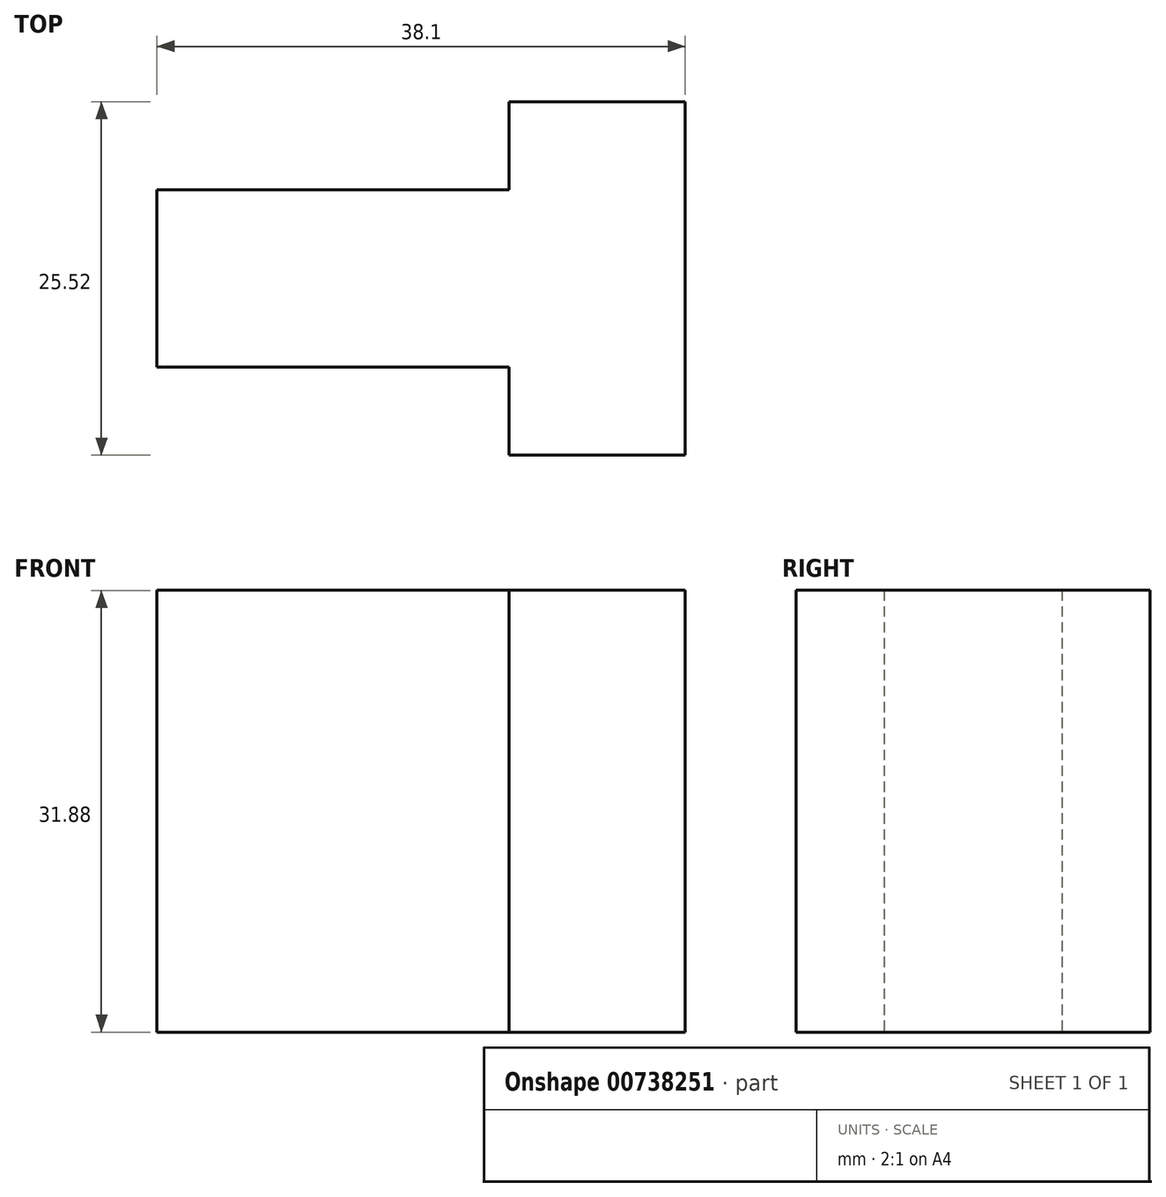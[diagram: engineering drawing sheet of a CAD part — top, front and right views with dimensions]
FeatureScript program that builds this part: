
annotation { "Feature Type Name" : "Feature", "Feature Type Description" : "" }
export const myFeature = defineFeature(function(context is Context, id is Id, definition is map)
    precondition{}
    {
        {
            var Q0;
            Q0=qCreatedBy(makeId("Right.planeOp"),FACE);
            var sketch = newSketch(context, id + "F0", { "sketchPlane" : qUnion([Q0])});
            skLineSegment(sketch, "E0", {"start": v(25.73, 0) * mm, "end": v(38.55, 0) * mm});
            skLineSegment(sketch, "E1", {"start": v(25.73, 0) * mm, "end": v(25.73, 31.88) * mm});
            skLineSegment(sketch, "E2", {"start": v(38.55, 0) * mm, "end": v(38.55, 31.88) * mm});
            skLineSegment(sketch, "E3", {"start": v(38.55, 31.88) * mm, "end": v(25.73, 31.88) * mm});
            skSolve(sketch);
        }
        {
            var Q0;
            Q0 = qSketchRegion(id + "F0", true);
            extrude(context, id + "F1", {"entities" : qUnion([Q0]), "depth" : 38.1 * mm, "offsetDistance" : 25.4 * mm});
        }
        {
            var Q0;
            Q0=makeQuery(id+"F1.opExtrude","SWEPT_FACE",FACE,{"disambiguationData":[OSD([sQuery(id+"F0.wireOp",EDGE,"E2")])]});
            var sketch = newSketch(context, id + "F2", { "sketchPlane" : qUnion([Q0])});
            skLineSegment(sketch, "E4", {"start": v(-38.1, 31.88) * mm, "end": v(-25.39, 31.88) * mm});
            skLineSegment(sketch, "E5", {"start": v(-25.39, 31.88) * mm, "end": v(-25.39, 0) * mm});
            skLineSegment(sketch, "E6", {"start": v(-25.39, 0) * mm, "end": v(-38.1, 0) * mm});
            skLineSegment(sketch, "E7", {"start": v(-38.1, 0) * mm, "end": v(-38.1, 31.88) * mm});
            skSolve(sketch);
        }
        {
            var Q0;
            Q0 = qSketchRegion(id + "F2", true);
            extrude(context, id + "F3", {"entities" : qUnion([Q0]), "operationType" : NewBodyOperationType.ADD, "depth" : 6.35 * mm, "offsetDistance" : 25.4 * mm});
        }
        {
            var Q0;
            Q0=makeQuery(id+"F1.opExtrude","SWEPT_FACE",FACE,{"disambiguationData":[OSD([sQuery(id+"F0.wireOp",EDGE,"E1")])]});
            var sketch = newSketch(context, id + "F4", { "sketchPlane" : qUnion([Q0])});
            skLineSegment(sketch, "E8", {"start": v(38.1, 31.88) * mm, "end": v(25.39, 31.88) * mm});
            skLineSegment(sketch, "E9", {"start": v(25.39, 31.88) * mm, "end": v(25.39, 0) * mm});
            skLineSegment(sketch, "E10", {"start": v(25.39, 0) * mm, "end": v(38.1, 0) * mm});
            skLineSegment(sketch, "E11", {"start": v(38.1, 0) * mm, "end": v(38.1, 31.88) * mm});
            skSolve(sketch);
        }
        {
            var Q0;
            Q0 = qSketchRegion(id + "F4", true);
            extrude(context, id + "F5", {"entities" : qUnion([Q0]), "operationType" : NewBodyOperationType.ADD, "depth" : 6.35 * mm, "offsetDistance" : 25.4 * mm});
        }
    });
